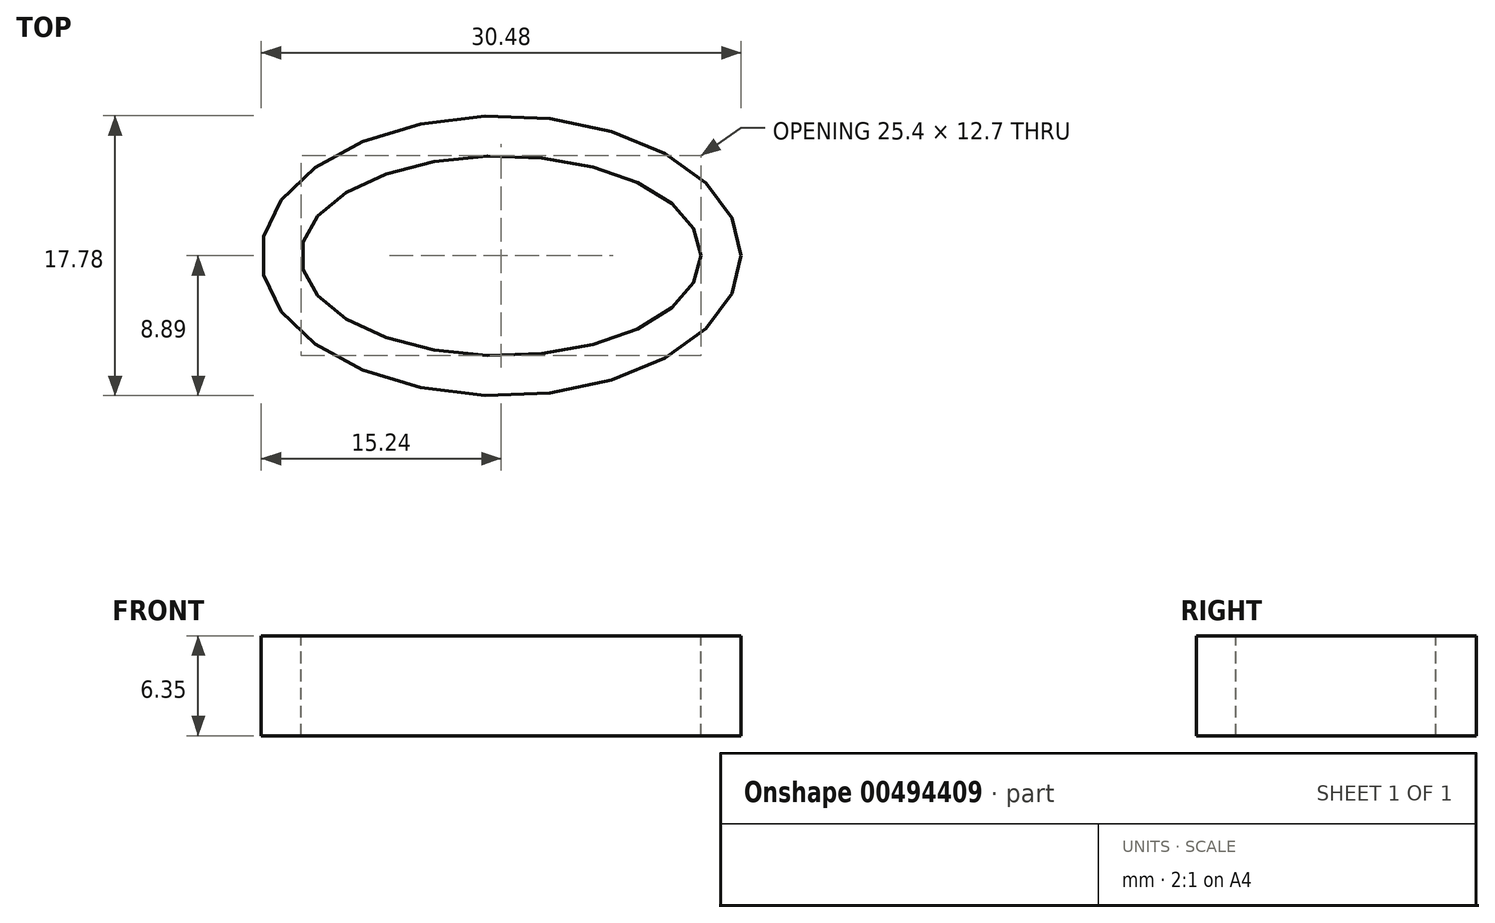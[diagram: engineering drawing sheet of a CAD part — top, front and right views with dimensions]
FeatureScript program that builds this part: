
annotation { "Feature Type Name" : "Feature", "Feature Type Description" : "" }
export const myFeature = defineFeature(function(context is Context, id is Id, definition is map)
    precondition{}
    {
        {
            var Q0;
            Q0=qCreatedBy(makeId("Top.planeOp"),FACE);
            var sketch = newSketch(context, id + "F0", { "sketchPlane" : qUnion([Q0])});
            skEllipse(sketch, "E0", {"center": v(0, 0) * mm, "majorRadius": 12.7 * mm, "minorRadius": 6.35 * mm, "majorAxis": v(1, 0)});
            skEllipse(sketch, "E1", {"center": v(0, 0) * mm, "majorRadius": 15.24 * mm, "minorRadius": 8.9 * mm, "majorAxis": v(1, 0)});
            skSolve(sketch);
        }
        {
            var Q0;
            Q0=makeQuery(id+"F0.imprint","IMPRINT",FACE,{"disambiguationData":[TD([[makeQuery(id+"F0.imprint","IMPRINT",EDGE,{"derivedFrom":sQuery(id+"F0.wireOp",EDGE,"E0")}),-1.0]])]});
            extrude(context, id + "F1", {"entities" : qUnion([Q0]), "oppositeDirection" : true, "depth" : 6.35 * mm, "offsetDistance" : 25.4 * mm});
        }
    });
